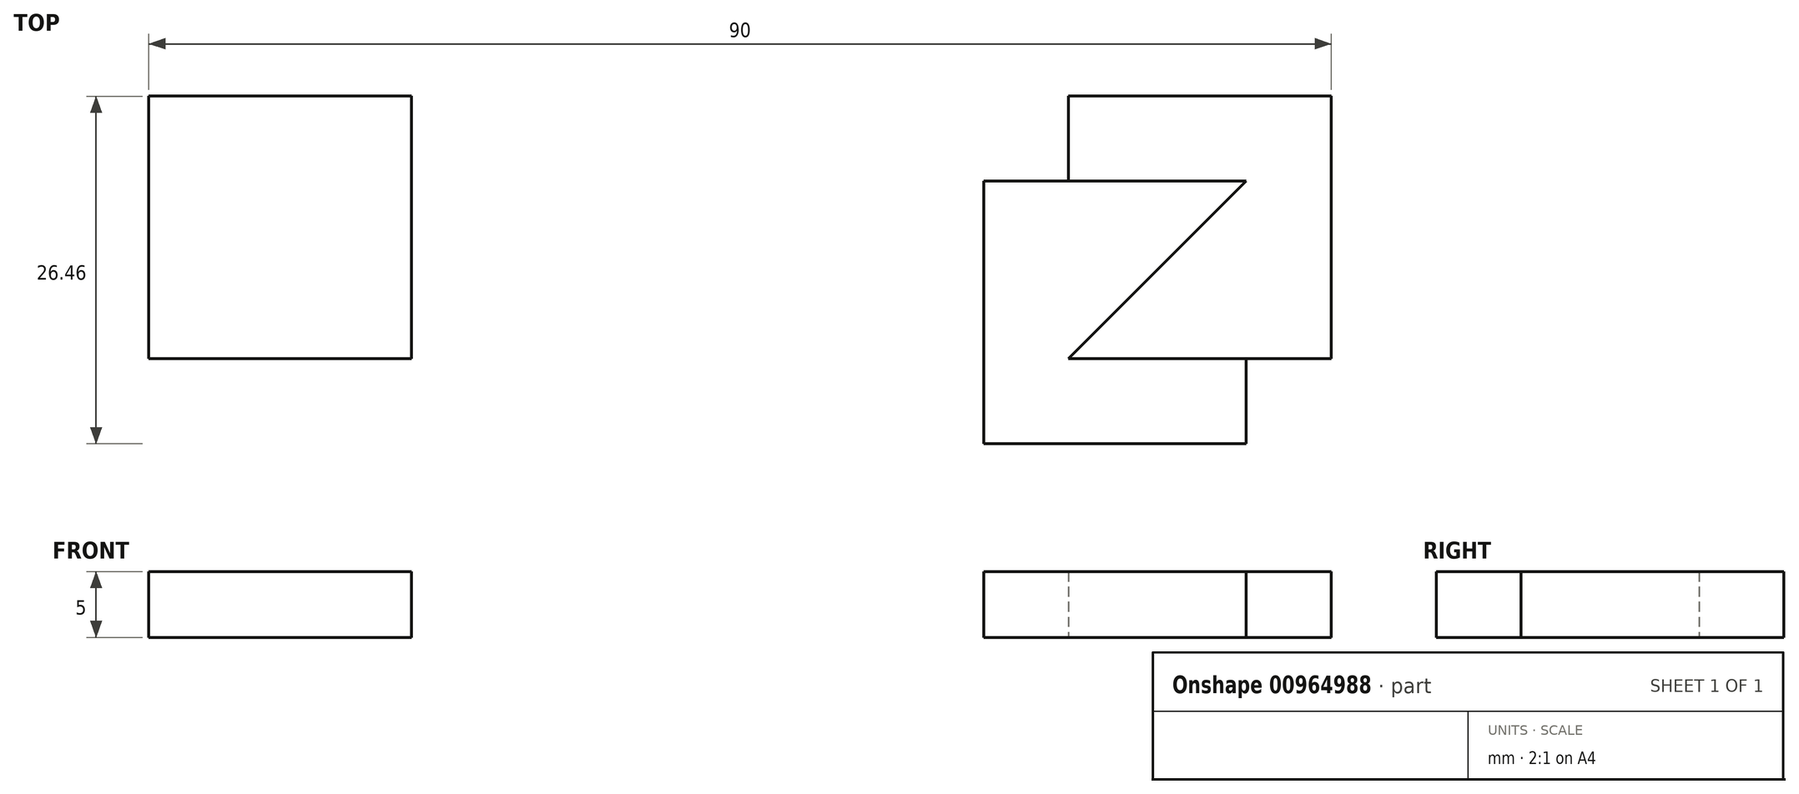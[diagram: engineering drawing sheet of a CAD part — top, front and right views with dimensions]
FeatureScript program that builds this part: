
annotation { "Feature Type Name" : "Feature", "Feature Type Description" : "" }
export const myFeature = defineFeature(function(context is Context, id is Id, definition is map)
    precondition{}
    {
        {
            var Q0;
            Q0=qCreatedBy(makeId("Top.planeOp"),FACE);
            var sketch = newSketch(context, id + "F0", { "sketchPlane" : qUnion([Q0])});
            skLineSegment(sketch, "E0.bottom", {"start": v(10, -10) * mm, "end": v(-10, -10) * mm});
            skLineSegment(sketch, "E0.top", {"start": v(10, 10) * mm, "end": v(-10, 10) * mm});
            skLineSegment(sketch, "E0.left", {"start": v(10, -10) * mm, "end": v(10, 10) * mm});
            skLineSegment(sketch, "E0.right", {"start": v(-10, -10) * mm, "end": v(-10, 10) * mm});
            skPoint(sketch, "E0.middle", {"position": v(0, 0) * mm});
            skLineSegment(sketch, "E1", {"start": v(-10, -10) * mm, "end": v(10, 10) * mm, "construction": true});
            skPoint(sketch, "E2", {"position": v(6.46, 6.46) * mm});
            skLineSegment(sketch, "E3.bottom", {"start": v(16.46, -3.54) * mm, "end": v(-3.54, -3.54) * mm});
            skLineSegment(sketch, "E3.top", {"start": v(16.46, 16.46) * mm, "end": v(-3.54, 16.46) * mm});
            skLineSegment(sketch, "E3.left", {"start": v(16.46, -3.54) * mm, "end": v(16.46, 16.46) * mm});
            skLineSegment(sketch, "E3.right", {"start": v(-3.54, -3.54) * mm, "end": v(-3.54, 16.46) * mm});
            skLineSegment(sketch, "E4", {"start": v(-3.54, -3.54) * mm, "end": v(10, 10) * mm});
            skLineSegment(sketch, "E5.bottom", {"start": v(-73.54, 16.46) * mm, "end": v(-53.54, 16.46) * mm});
            skLineSegment(sketch, "E5.top", {"start": v(-73.54, -3.54) * mm, "end": v(-53.54, -3.54) * mm});
            skLineSegment(sketch, "E5.left", {"start": v(-73.54, 16.46) * mm, "end": v(-73.54, -3.54) * mm});
            skLineSegment(sketch, "E5.right", {"start": v(-53.54, 16.46) * mm, "end": v(-53.54, -3.54) * mm});
            skSolve(sketch);
        }
        {
            var Q0;
            {var subQ1=sQuery(id+"F0.wireOp",EDGE,"E0.bottom");Q0=makeQuery(id+"F0.imprint","IMPRINT",FACE,{"disambiguationData":[TD([[makeQuery(id+"F0.imprint","IMPRINT",EDGE,{"derivedFrom":subQ1}),-1.0]])]});}
            var Q1;
            {var subQ0=sQuery(id+"F0.wireOp",EDGE,"E4");Q1=makeQuery(id+"F0.imprint","IMPRINT",FACE,{"disambiguationData":[TD([[makeQuery(id+"F0.imprint","IMPRINT",EDGE,{"derivedFrom":subQ0}),1.0]])]});}
            extrude(context, id + "F1", {"entities" : qUnion([Q0, Q1]), "depth" : 5 * mm, "offsetDistance" : 25 * mm});
        }
        {
            var Q0;
            {var subQ0=sQuery(id+"F0.wireOp",EDGE,"E4");Q0=makeQuery(id+"F0.imprint","IMPRINT",FACE,{"disambiguationData":[TD([[makeQuery(id+"F0.imprint","IMPRINT",EDGE,{"derivedFrom":subQ0}),-1.0]])]});}
            var Q1;
            {var subQ0=sQuery(id+"F0.wireOp",EDGE,"E3.top");Q1=makeQuery(id+"F0.imprint","IMPRINT",FACE,{"disambiguationData":[TD([[makeQuery(id+"F0.imprint","IMPRINT",EDGE,{"derivedFrom":subQ0}),1.0]])]});}
            extrude(context, id + "F2", {"entities" : qUnion([Q0, Q1]), "depth" : 5 * mm, "offsetDistance" : 25 * mm});
        }
        {
            var Q0;
            Q0=makeQuery(id+"F0.imprint","IMPRINT",FACE,{"disambiguationData":[TD([[makeQuery(id+"F0.imprint","IMPRINT",EDGE,{"derivedFrom":sQuery(id+"F0.wireOp",EDGE,"E5.bottom")}),-1.0]])]});
            extrude(context, id + "F3", {"entities" : qUnion([Q0]), "depth" : 5 * mm, "offsetDistance" : 25 * mm});
        }
    });
